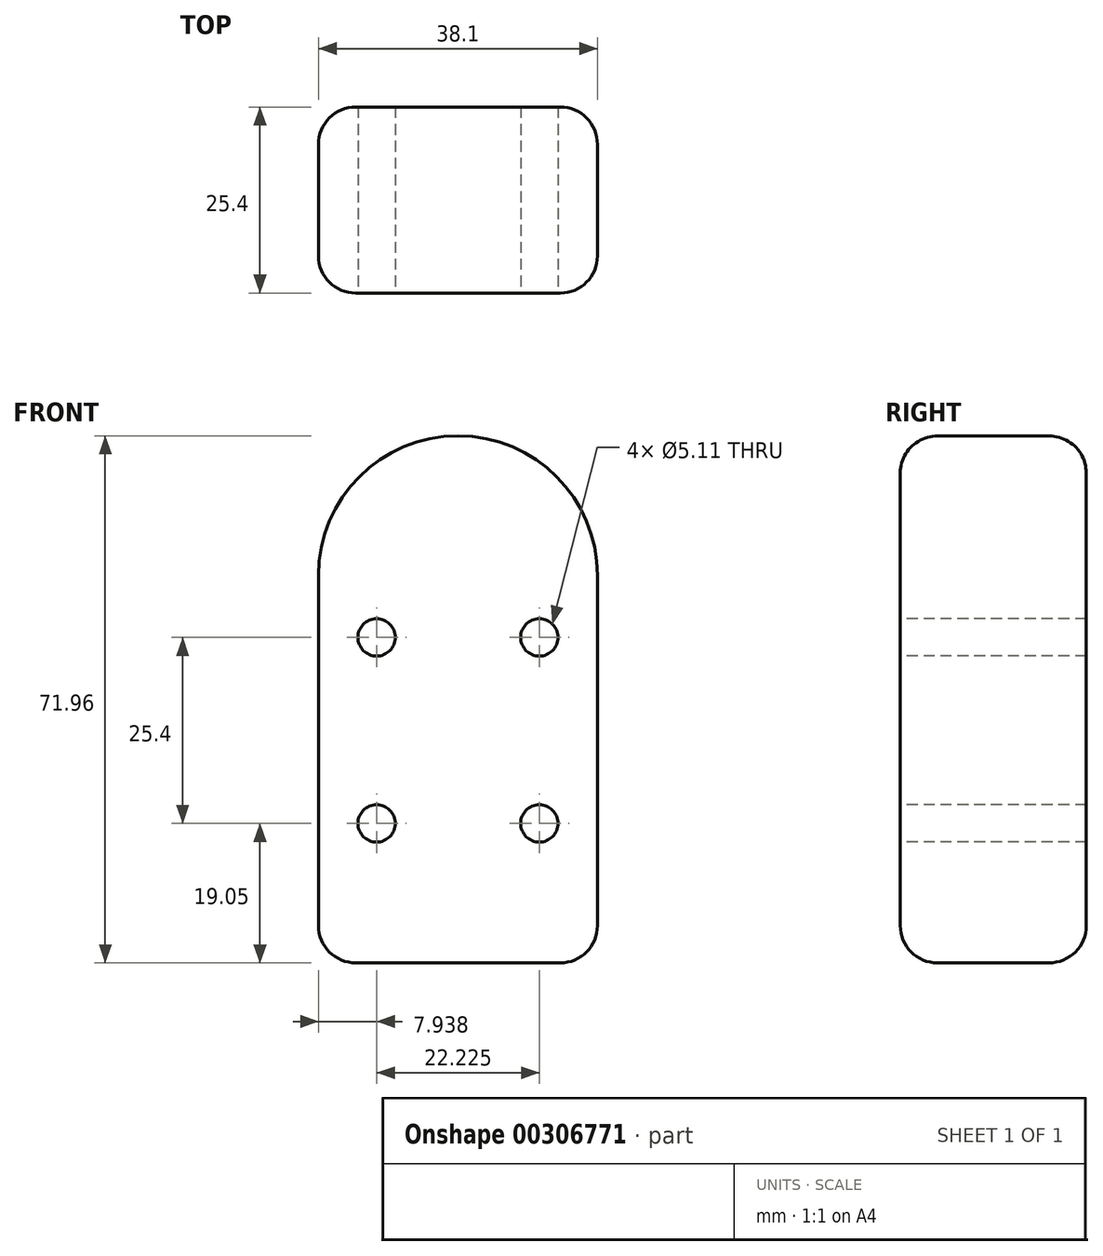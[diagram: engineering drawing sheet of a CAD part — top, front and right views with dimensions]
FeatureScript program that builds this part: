
annotation { "Feature Type Name" : "Feature", "Feature Type Description" : "" }
export const myFeature = defineFeature(function(context is Context, id is Id, definition is map)
    precondition{}
    {
        {
            var Q0;
            Q0=qCreatedBy(makeId("Front.planeOp"),FACE);
            var sketch = newSketch(context, id + "F0", { "sketchPlane" : qUnion([Q0])});
            skLineSegment(sketch, "E0", {"start": v(0, 38.16) * mm, "end": v(0, -34.7) * mm, "construction": true});
            skArc(sketch, "E1", {"start": v(19.05, 52.91) * mm, "mid": v(0, 71.96) * mm, "end": v(-19.05, 52.91) * mm});
            skLineSegment(sketch, "E2", {"start": v(-19.05, 52.91) * mm, "end": v(-19.05, 0) * mm});
            skLineSegment(sketch, "E3.MirrorCS", {"start": v(19.05, 52.91) * mm, "end": v(19.05, 0) * mm});
            skLineSegment(sketch, "E4", {"start": v(-19.05, 0) * mm, "end": v(19.05, 0) * mm});
            skSolve(sketch);
        }
        {
            var Q0;
            Q0 = qSketchRegion(id + "F0", true);
            extrude(context, id + "F1", {"entities" : qUnion([Q0]), "depth" : 25.4 * mm});
        }
        {
            var Q0;
            Q0=makeQuery(id+"F1.opExtrude","CAP_FACE",FACE,{"disambiguationData":[OSD([sQuery(id+"F0.wireOp",EDGE,"E1"),sQuery(id+"F0.wireOp",EDGE,"E2"),sQuery(id+"F0.wireOp",EDGE,"E3.MirrorCS"),sQuery(id+"F0.wireOp",EDGE,"E4")])],"isStart":false});
            var sketch = newSketch(context, id + "F2", { "sketchPlane" : qUnion([Q0])});
            skPoint(sketch, "E5", {"position": v(-11.11, 44.45) * mm});
            skPoint(sketch, "E6", {"position": v(-11.11, 19.05) * mm});
            skLineSegment(sketch, "E7", {"start": v(0, 64.9) * mm, "end": v(0, 5.74) * mm, "construction": true});
            skPoint(sketch, "E8.MirrorP", {"position": v(11.11, 44.45) * mm});
            skPoint(sketch, "E9.MirrorP", {"position": v(11.11, 19.05) * mm});
            skSolve(sketch);
        }
        {
            var Q0;
            Q0=sQuery(id+"F2.wireOp",VERTEX,"E5");
            var Q1;
            Q1=sQuery(id+"F2.wireOp",VERTEX,"E8.MirrorP");
            var Q2;
            Q2=sQuery(id+"F2.wireOp",VERTEX,"E9.MirrorP");
            var Q3;
            Q3=sQuery(id+"F2.wireOp",VERTEX,"E6");
            var Q4;
            Q4=makeQuery(id+"F1.opExtrude","SWEPT_BODY",BODY,{"disambiguationData":[OSD([sQuery(id+"F0.wireOp",EDGE,"E1"),sQuery(id+"F0.wireOp",EDGE,"E2"),sQuery(id+"F0.wireOp",EDGE,"E3.MirrorCS"),sQuery(id+"F0.wireOp",EDGE,"E4")])]});
            hole(context, id + "F3", {"style" : HoleStyle.SIMPLE, "endStyle" : HoleEndStyle.THROUGH, "standardTappedOrClearance" : lookupTablePath({ "standard" : "ANSI", "engagement" : "75%", "pitch" : "20 tpi", "size" : "1/4", "type" : "Tapped" }), "standardBlindInLast" : lookupTablePath({ "standard" : "ANSI", "engagement" : "75%", "pitch" : "20 tpi", "size" : "1/4", "type" : "Tapped" }), "holeDiameter" : 5.1 * mm, "showTappedDepth" : true, "tappedDepth" : 12.7 * mm, "tapClearance" : 3, "locations" : qUnion([Q0, Q1, Q2, Q3]), "scope" : qUnion([Q4]), "majorDiameter" : 6.35 * mm});
        }
        {
            var Q0;
            Q0=makeQuery(id+"F1.opExtrude","SWEPT_EDGE",EDGE,{"disambiguationData":[OSD([sQuery(id+"F0.wireOp",EDGE,"E2"),sQuery(id+"F0.wireOp",EDGE,"E4")])]});
            var Q1;
            Q1=makeQuery(id+"F1.opExtrude","SWEPT_EDGE",EDGE,{"disambiguationData":[OSD([sQuery(id+"F0.wireOp",EDGE,"E3.MirrorCS"),sQuery(id+"F0.wireOp",EDGE,"E4")])]});
            fillet(context, id + "F4", {"entities" : qUnion([Q0, Q1]), "radius" : 5.08 * mm, "tangentPropagation" : true, "allowEdgeOverflow" : false});
        }
        {
            var Q0;
            Q0=makeQuery(id+"F1.opExtrude","CAP_EDGE",EDGE,{"disambiguationData":[OSD([sQuery(id+"F0.wireOp",EDGE,"E2")])],"isStart":false});
            var Q1;
            Q1=makeQuery(id+"F1.opExtrude","CAP_EDGE",EDGE,{"disambiguationData":[OSD([sQuery(id+"F0.wireOp",EDGE,"E4")])],"isStart":false});
            var Q2;
            Q2=makeQuery(id+"F1.opExtrude","CAP_EDGE",EDGE,{"disambiguationData":[OSD([sQuery(id+"F0.wireOp",EDGE,"E4")])],"isStart":true});
            var Q3;
            Q3=makeQuery(id+"F1.opExtrude","CAP_EDGE",EDGE,{"disambiguationData":[OSD([sQuery(id+"F0.wireOp",EDGE,"E3.MirrorCS")])],"isStart":true});
            fillet(context, id + "F5", {"entities" : qUnion([Q0, Q1, Q2, Q3]), "radius" : 5.08 * mm, "tangentPropagation" : true, "allowEdgeOverflow" : false});
        }
    });
